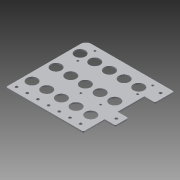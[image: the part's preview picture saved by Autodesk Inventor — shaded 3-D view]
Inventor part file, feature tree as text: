
AUTODESK INVENTOR PART (.ipt)
format: ipt  version: 2014 SP1 (Build 180222100, 222)  size: 198,144 bytes
history: native  units: in
note: dims shown in document units (in); Inventor stores cm internally (conversion verified against a paired STEP export)
features: reference x11, extrude x1, fillet x1, sketch x1
ambient origin geometry x8: Origin, YZ Plane, XZ Plane, XY Plane, X Axis, Y Axis, Z Axis, Center Point
bodies: Solid1 (feature_tree)
feature tree (14):
  extrude  "Extrusion1"  Depth=2.0in
  fillet  "Fillet1"  Radius=0.125in
  sketch  "Sketch1"  dims[d8=1.86in d9=0.2in d12=0.125in d13=0.0in d20=0.125in d21=1.42in d23=0.2in d24=0.5in d26=8.25in d29=1.375in d30=3.0in d31=7.5in d35=1.61in d37=1.25in d39=5.5105in d40=0.5in d41=1.0in d43=2.0in d44=1.9685in d46=1.375in d47=1.1811in d49=2.25in d52=1.305in]
  reference  "Reference7"
  reference  "Reference8"
  reference  "Reference9"
  reference  "Reference10"
  reference  "Reference11"
  reference  "Reference12"
  reference  "Reference13"
  reference  "Reference14"
  reference  "Reference15"
  reference  "Reference16"
  reference  "Reference17"
